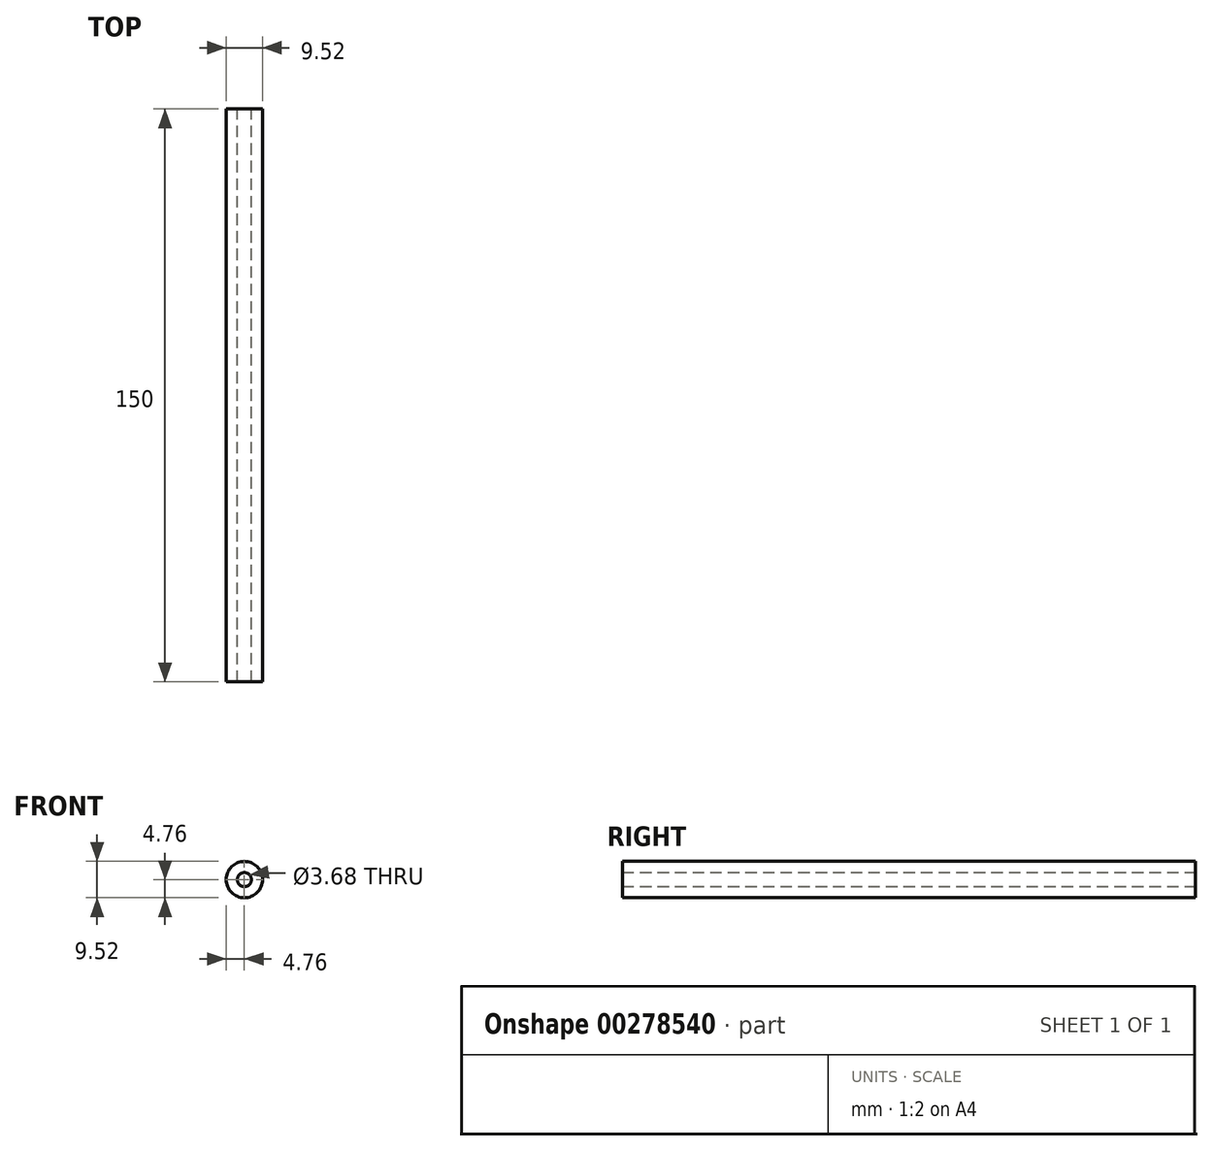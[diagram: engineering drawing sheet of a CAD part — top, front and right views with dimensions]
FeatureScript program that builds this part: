
annotation { "Feature Type Name" : "Feature", "Feature Type Description" : "" }
export const myFeature = defineFeature(function(context is Context, id is Id, definition is map)
    precondition{}
    {
        {
            var Q0;
            Q0=qCreatedBy(makeId("Front.planeOp"),FACE);
            var sketch = newSketch(context, id + "F0", { "sketchPlane" : qUnion([Q0])});
            skCircle(sketch, "E0", {"center": v(0, 0) * mm, "radius": 4.76 * mm});
            skCircle(sketch, "E1", {"center": v(0, 0) * mm, "radius": 1.84 * mm});
            skSolve(sketch);
        }
        {
            var Q0;
            Q0 = qSketchRegion(id + "F0", true);
            var Q1;
            Q1=sQuery(id+"F0.wireOp",EDGE,"E0");
            extrude(context, id + "F1", {"entities" : qUnion([Q0]), "surfaceEntities" : qUnion([Q1]), "depth" : 150 * mm});
        }
    });
